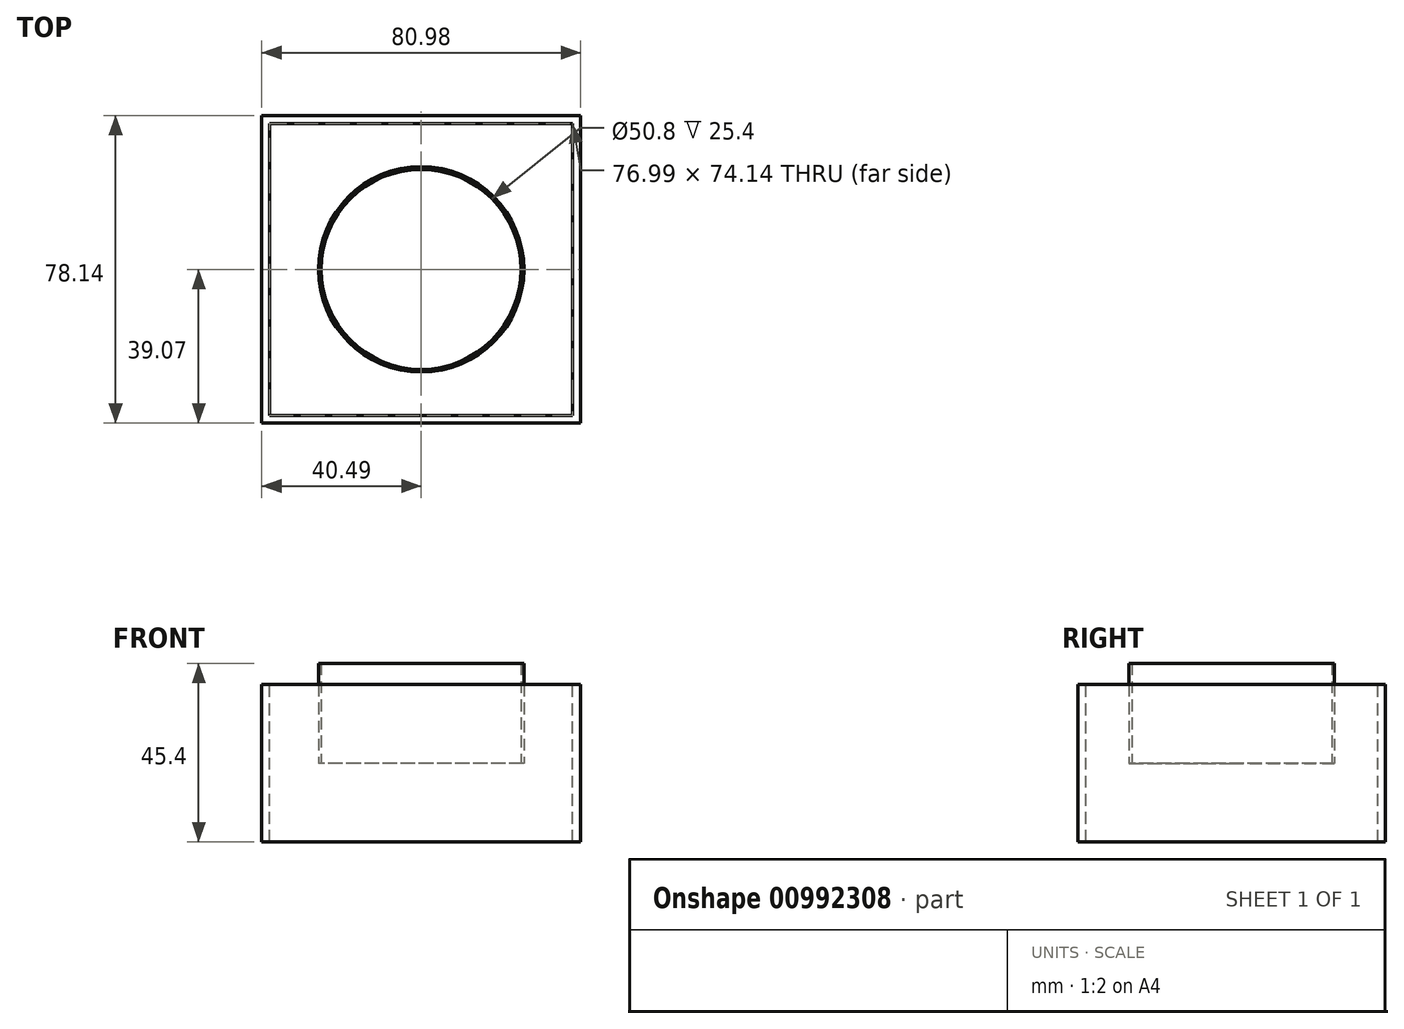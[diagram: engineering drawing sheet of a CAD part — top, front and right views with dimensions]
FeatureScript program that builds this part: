
annotation { "Feature Type Name" : "Feature", "Feature Type Description" : "" }
export const myFeature = defineFeature(function(context is Context, id is Id, definition is map)
    precondition{}
    {
        {
            var Q0;
            Q0=qCreatedBy(makeId("Top.planeOp"),FACE);
            var sketch = newSketch(context, id + "F0", { "sketchPlane" : qUnion([Q0])});
            skLineSegment(sketch, "E0.bottom", {"start": v(38.5, 37.07) * mm, "end": v(-38.5, 37.07) * mm});
            skLineSegment(sketch, "E0.top", {"start": v(38.5, -37.07) * mm, "end": v(-38.5, -37.07) * mm});
            skLineSegment(sketch, "E0.left", {"start": v(38.5, 37.07) * mm, "end": v(38.5, -37.07) * mm});
            skLineSegment(sketch, "E0.right", {"start": v(-38.5, 37.07) * mm, "end": v(-38.5, -37.07) * mm});
            skPoint(sketch, "E0.middle", {"position": v(0, 0) * mm});
            skLineSegment(sketch, "E1.0", {"start": v(40.5, 39.07) * mm, "end": v(-40.5, 39.07) * mm});
            skLineSegment(sketch, "E1.1", {"start": v(40.5, 39.07) * mm, "end": v(40.5, -39.07) * mm});
            skLineSegment(sketch, "E1.2", {"start": v(40.5, -39.07) * mm, "end": v(-40.5, -39.07) * mm});
            skLineSegment(sketch, "E1.3", {"start": v(-40.5, 39.07) * mm, "end": v(-40.5, -39.07) * mm});
            skSolve(sketch);
        }
        {
            var Q0;
            Q0=makeQuery(id+"F0.imprint","IMPRINT",FACE,{"disambiguationData":[TD([[makeQuery(id+"F0.imprint","IMPRINT",EDGE,{"derivedFrom":sQuery(id+"F0.wireOp",EDGE,"E0.bottom")}),-1.0]])]});
            extrude(context, id + "F1", {"entities" : qUnion([Q0]), "oppositeDirection" : true, "depth" : 20 * mm, "offsetDistance" : 25.4 * mm, "hasSecondDirection" : true, "secondDirectionOppositeDirection" : false, "secondDirectionDepth" : 20 * mm});
        }
        {
            var Q0;
            Q0=qCreatedBy(makeId("Top.planeOp"),FACE);
            var sketch = newSketch(context, id + "F2", { "sketchPlane" : qUnion([Q0])});
            skCircle(sketch, "E2", {"center": v(0, 0) * mm, "radius": 25.4 * mm});
            skCircle(sketch, "E3", {"center": v(0, 0) * mm, "radius": 0.39 * mm});
            skCircle(sketch, "E4.0", {"center": v(0, 0) * mm, "radius": 26.1 * mm});
            skSolve(sketch);
        }
        {
            var Q0;
            Q0 = qSketchRegion(id + "F2", true);
            extrude(context, id + "F3", {"entities" : qUnion([Q0]), "depth" : 25.4 * mm, "offsetDistance" : 25.4 * mm});
        }
    });
